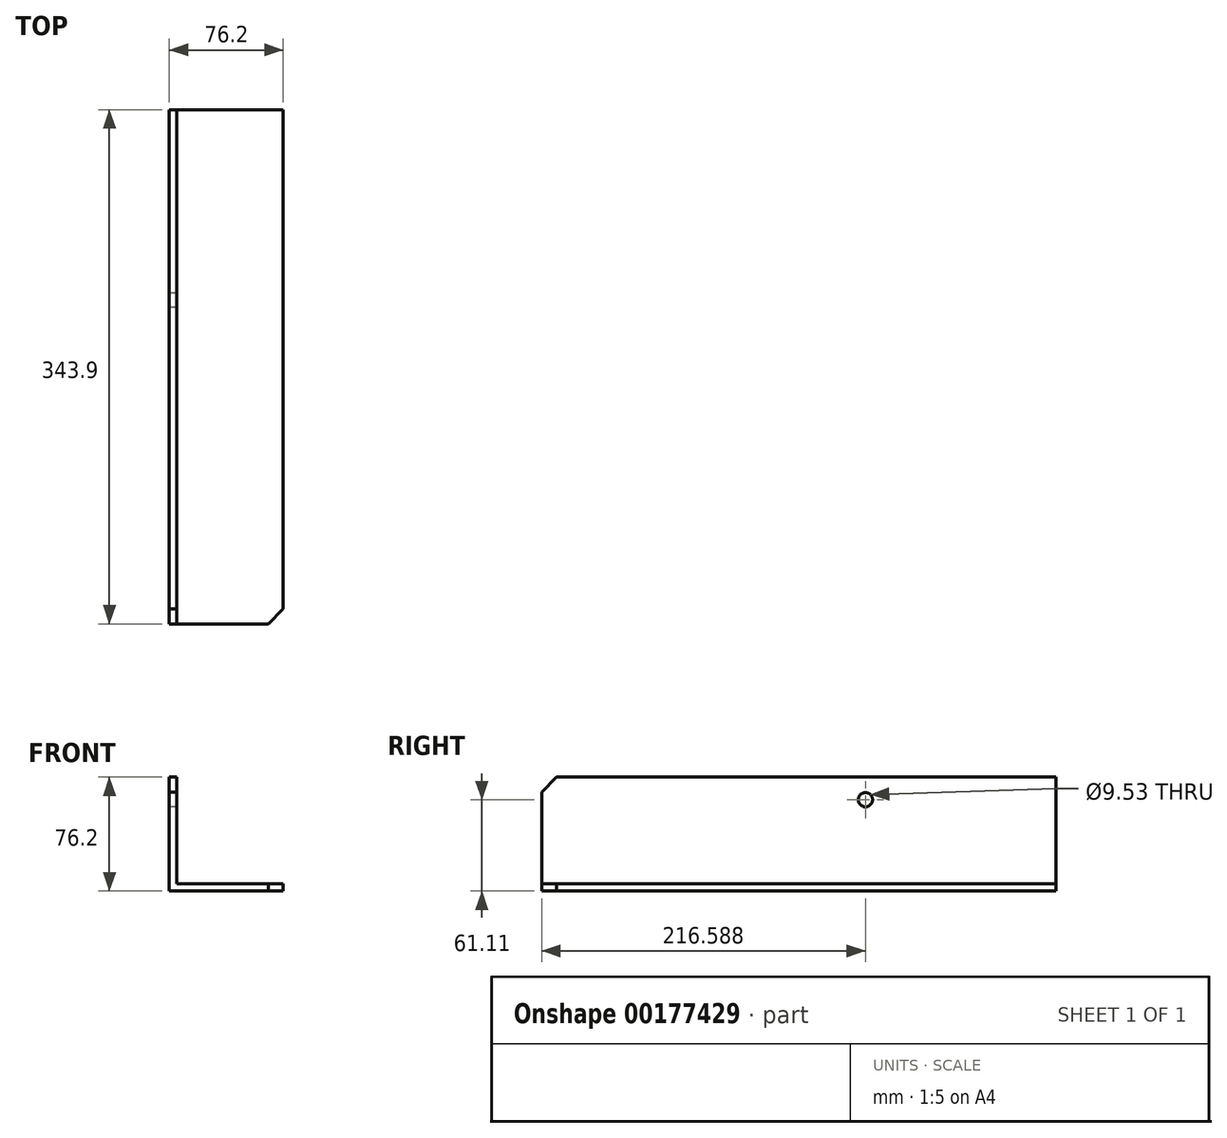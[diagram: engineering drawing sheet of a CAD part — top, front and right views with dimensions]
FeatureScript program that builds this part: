
annotation { "Feature Type Name" : "Feature", "Feature Type Description" : "" }
export const myFeature = defineFeature(function(context is Context, id is Id, definition is map)
    precondition{}
    {
        {
            var Q0;
            Q0=qCreatedBy(makeId("Front.planeOp"),FACE);
            var sketch = newSketch(context, id + "F0", { "sketchPlane" : qUnion([Q0])});
            skLineSegment(sketch, "E0", {"start": v(0, 0) * mm, "end": v(76.2, 0) * mm});
            skLineSegment(sketch, "E1", {"start": v(0, 0) * mm, "end": v(0, 76.2) * mm});
            skLineSegment(sketch, "E2.0", {"start": v(5, 5) * mm, "end": v(5, 76.2) * mm});
            skLineSegment(sketch, "E2.1", {"start": v(5, 5) * mm, "end": v(76.2, 5) * mm});
            skLineSegment(sketch, "E3", {"start": v(0, 76.2) * mm, "end": v(5, 76.2) * mm});
            skLineSegment(sketch, "E4", {"start": v(76.2, 0) * mm, "end": v(76.2, 5) * mm});
            skSolve(sketch);
        }
        {
            var Q0;
            Q0=makeQuery(id+"F0.imprint","IMPRINT",FACE,{"disambiguationData":[TD([[makeQuery(id+"F0.imprint","IMPRINT",EDGE,{"derivedFrom":sQuery(id+"F0.wireOp",EDGE,"E0")}),1.0]])]});
            extrude(context, id + "F1", {"entities" : qUnion([Q0]), "depth" : 343.9 * mm});
        }
        {
            var Q0;
            Q0=makeQuery(id+"F1.opExtrude","SWEPT_FACE",FACE,{"disambiguationData":[OSD([sQuery(id+"F0.wireOp",EDGE,"E1")])]});
            var sketch = newSketch(context, id + "F2", { "sketchPlane" : qUnion([Q0])});
            skLineSegment(sketch, "E5.0", {"start": v(127.31, 0) * mm, "end": v(127.31, 76.2) * mm});
            skLineSegment(sketch, "E6.0", {"start": v(5, 71.2) * mm, "end": v(5, 5) * mm});
            skLineSegment(sketch, "E6.1", {"start": v(338.9, 71.2) * mm, "end": v(5, 71.2) * mm});
            skLineSegment(sketch, "E6.2", {"start": v(338.9, 5) * mm, "end": v(338.9, 71.2) * mm});
            skLineSegment(sketch, "E6.3", {"start": v(5, 5) * mm, "end": v(338.9, 5) * mm});
            skLineSegment(sketch, "E7.0", {"start": v(343.9, 61.1) * mm, "end": v(0, 61.1) * mm});
            skPoint(sketch, "E8", {"position": v(127.31, 61.1) * mm});
            skSolve(sketch);
        }
        {
            var Q0;
            Q0=sQuery(id+"F2.wireOp",VERTEX,"E8");
            var Q1;
            Q1=makeQuery(id+"F1.opExtrude","SWEPT_BODY",BODY,{"disambiguationData":[OSD([sQuery(id+"F0.wireOp",EDGE,"E0"),sQuery(id+"F0.wireOp",EDGE,"E1"),sQuery(id+"F0.wireOp",EDGE,"E2.0"),sQuery(id+"F0.wireOp",EDGE,"E2.1"),sQuery(id+"F0.wireOp",EDGE,"E3"),sQuery(id+"F0.wireOp",EDGE,"E4")])]});
            hole(context, id + "F3", {"style" : HoleStyle.SIMPLE, "endStyle" : HoleEndStyle.THROUGH, "holeDiameter" : 9.53 * mm, "locations" : qUnion([Q0]), "scope" : qUnion([Q1]), "isTappedThrough" : true});
        }
        {
            var Q0;
            Q0=makeQuery(id+"F1.opExtrude","CAP_EDGE",EDGE,{"disambiguationData":[OSD([sQuery(id+"F0.wireOp",EDGE,"E4")])],"isStart":false});
            var Q1;
            Q1=makeQuery(id+"F1.opExtrude","CAP_EDGE",EDGE,{"disambiguationData":[OSD([sQuery(id+"F0.wireOp",EDGE,"E3")])],"isStart":false});
            chamfer(context, id + "F4", {"entities" : qUnion([Q0, Q1]), "width" : 10 * mm, "tangentPropagation" : true});
        }
    });
